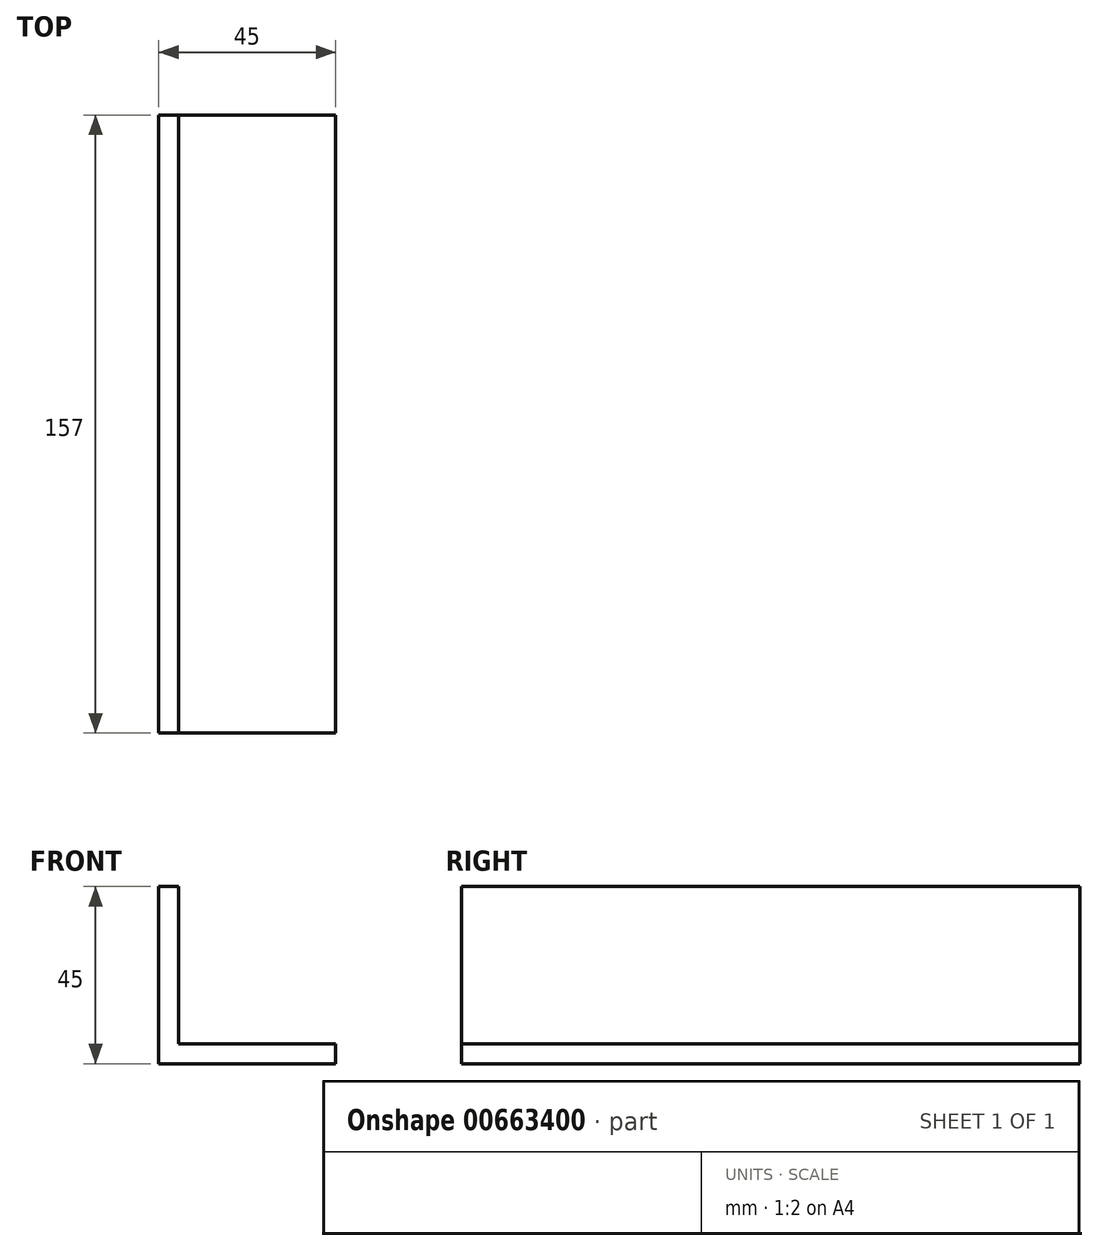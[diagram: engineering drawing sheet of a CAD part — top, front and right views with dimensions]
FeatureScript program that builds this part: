
annotation { "Feature Type Name" : "Feature", "Feature Type Description" : "" }
export const myFeature = defineFeature(function(context is Context, id is Id, definition is map)
    precondition{}
    {
        {
            var Q0;
            Q0=qCreatedBy(makeId("Front.planeOp"),FACE);
            var sketch = newSketch(context, id + "F0", { "sketchPlane" : qUnion([Q0])});
            skLineSegment(sketch, "E0", {"start": v(0, 0) * mm, "end": v(0, 45) * mm});
            skLineSegment(sketch, "E1", {"start": v(0, 0) * mm, "end": v(45, 0) * mm});
            skLineSegment(sketch, "E2.0", {"start": v(5, 5) * mm, "end": v(45, 5) * mm});
            skLineSegment(sketch, "E2.1", {"start": v(5, 5) * mm, "end": v(5, 45) * mm});
            skLineSegment(sketch, "E3", {"start": v(45, 0) * mm, "end": v(45, 5) * mm});
            skLineSegment(sketch, "E4", {"start": v(0, 45) * mm, "end": v(5, 45) * mm});
            skSolve(sketch);
        }
        {
            var Q0;
            Q0=makeQuery(id+"F0.imprint","IMPRINT",FACE,{"disambiguationData":[TD([[makeQuery(id+"F0.imprint","IMPRINT",EDGE,{"derivedFrom":sQuery(id+"F0.wireOp",EDGE,"E0")}),-1.0]])]});
            extrude(context, id + "F1", {"entities" : qUnion([Q0]), "depth" : (165 - 8) * mm, "offsetDistance" : 25 * mm});
        }
    });
